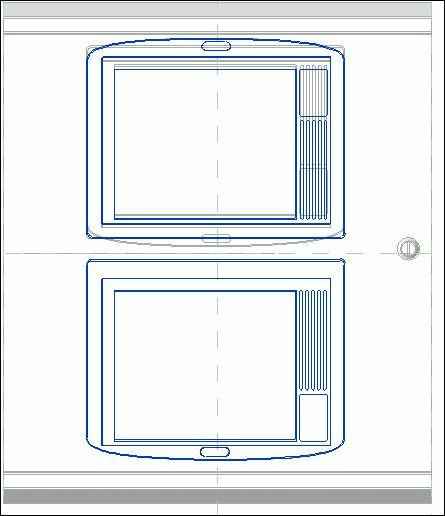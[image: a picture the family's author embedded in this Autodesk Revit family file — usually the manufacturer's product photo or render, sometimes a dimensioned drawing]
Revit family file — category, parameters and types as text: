
# Revit family: Tyco _ FPP  (FireClass) FC700 series _  Addressable Control and Indicating Panels____
name_source: partatom
category: Fire Alarm Devices
revit_build: Autodesk Revit 2016 (Build: 20150714_1515(x64)
units: mm (PartAtom-declared; Revit-internal decimal feet)

## family parameters
Always vertical = Yes
Cut with Voids When Loaded = No
Host = Wall
Maintain Annotation Orientation = No
OmniClass Number = 23.85.30.00
OmniClass Title = Safety and Security Information Systems
Part Type = Normal
Room Calculation Point = No
Round Connector Dimension = Use Diameter
Shared = No

## types (4) — shared parameters
Asset Type = Moveable
Brand = FireClass
Category = Ee_40_15_75
Duration Unit = Year
Has Protective Earth = TRUE
Installation Date = 1900-12-31T23:59:59
Manufacturer = Tyco Fire & Security GmbH
Manufacturer Name = Tyco Fire & Security GmbH
Manufacturer URL = www.zettlerfire.com
Material = Mild steel Zintec (Electro Zinc Coated)
NBS Description = Fire detection and alarm control and indicating equipment (CIE)
NBS Reference = 90-75-30/380
No Of Zones Supported = 240
Nominal Current = 2.2 A
Nominal Frequency Range = 50/60 Hz
Nominal Height = 480 mm  [stored 1.5748 ft]
Nominal Voltage = 230 V AC
Nominal Width = 410 mm  [stored 1.34514 ft]
Operation Temperature Range = -5 °C to +40 °C
Relative Humidity = 90% RH continuous (non-condensing)
Shape = Rectangle
Storage Temperature = -20 °C to +70 °C
URL = http://www.fireclass.net
Uniclass2 = Ee_40_15_75
Version = 1
Warranty Description = The 36 month warranty is applicable from the date of manufacture.
Warranty Duration Labor = 3
Warranty Duration Parts = 3 years
Warranty Duration Unit = Year
Warranty Start Date = 1900-12-31T23:59:59
zero-valued in all types: Expected Life, Replacement Cost

## per-type parameters (varying)
| type | Colour | Description | Double | No Of Zonal LEDs | Nominal Length | Number of Loops | Product Codes | Product Description | Product Specification | Single | Weight |
| FC702S | RAL 7035 | One HP or two SP Loop PROFILE Flexible Panel shallow housing | No | 16 | 140 mm  [stored 0.459318 ft] | 2 | 557.200.949 | FC702S 2 Loop FireClass panel | FireClass panel 2 shared power loops or 1 high power loop with maximum 250 addresses. TFT touchscreen display with 16 zonal LEDs. Compact housing 5 A PSU for 17 AH batteries. Networkable. | Yes | 9.7 kg |
| FC702D | RAL 7035 (Light Grey) | One HP or two SP Loop FireClass Panel deep housing | No | 16 | 205 mm  [stored 0.672572 ft] | 2 | 557.200.950 | FC702D 2 Loop FireClass panel | FireClass panel 2 shared power loops or 1 high power loop with maximum 250 addresses. TFT touchscreen display with 16 zonal LEDs.Designer housing 5 A PSU for 38AH batteries. Networkable. | Yes | 12.5 kg |
| FC708D | RAL 7035 (Light Grey) | Two HP or four SP loop, expandable to eight loop, FireClass Panel | Yes | 16 | 205 mm  [stored 0.672572 ft] | 4 | 557.200.951 | FC708D 4-8 Loop FireClass Panel | FireClass panel 4 shared power loops or 2 high power loops expandable to 8 shared power or 4 high power loops with maximum 1000 addresses. TFT touchscreen display with 80 zonal LEDs. Designer housing 5 A PSU for 38 AH batteries. Networkable. | No | 12.5 kg |
| FC718D | RAL 7035 (Light Grey) | Two HP or four SP loop, expandable to eight loop, FireClass Panel | No | 80 | 205 mm  [stored 0.672572 ft] | 4 | 557.200.952 | FC718D 4-8 Loop FireClass Panel | PROFILE Flexible panel 4 shared power loops or 2 high power loops expandable to 8 shared power or 4 high power loops with maximum 1000 addresses. TFT touchscreen display with 16 zonal LEDs. Designer housing 5 A PSU for 38 AH batteries. Networkable. | Yes | 13 kg |

note: column(s) folded — value = type name in every type: Model, Model Number, Name

note: [stored X ft] marks values corroborated as IEEE doubles in the binary element streams (Revit-internal decimal feet)

## geometry (parser evidence)
native form markers: Blend x2, Sweep x5
no freeform markers — native parametric forms only
